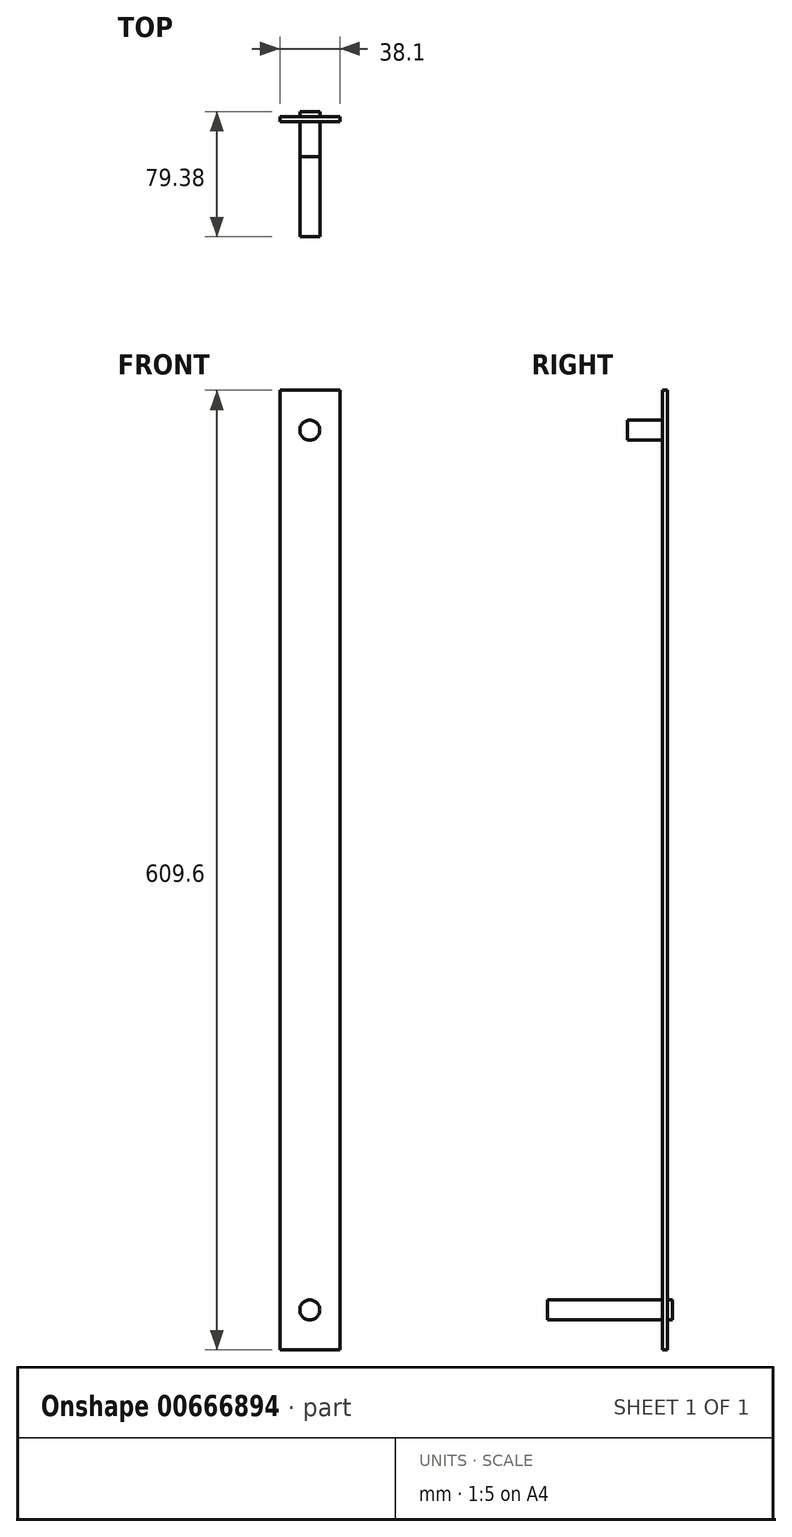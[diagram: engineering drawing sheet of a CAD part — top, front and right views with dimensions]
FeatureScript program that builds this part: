
annotation { "Feature Type Name" : "Feature", "Feature Type Description" : "" }
export const myFeature = defineFeature(function(context is Context, id is Id, definition is map)
    precondition{}
    {
        {
            var Q0;
            Q0=qCreatedBy(makeId("Front.planeOp"),FACE);
            var sketch = newSketch(context, id + "F0", { "sketchPlane" : qUnion([Q0])});
            skLineSegment(sketch, "E0.bottom", {"start": v(0, 0) * mm, "end": v(38.1, 0) * mm});
            skLineSegment(sketch, "E0.top", {"start": v(0, 609.6) * mm, "end": v(38.1, 609.6) * mm});
            skLineSegment(sketch, "E0.left", {"start": v(0, 0) * mm, "end": v(0, 609.6) * mm});
            skLineSegment(sketch, "E0.right", {"start": v(38.1, 0) * mm, "end": v(38.1, 609.6) * mm});
            skLineSegment(sketch, "E1", {"start": v(19.05, 609.6) * mm, "end": v(19.05, 0) * mm, "construction": true});
            skPoint(sketch, "E2", {"position": v(19.05, 25.4) * mm});
            skCircle(sketch, "E3", {"center": v(19.05, 25.4) * mm, "radius": 6.35 * mm});
            skPoint(sketch, "E4", {"position": v(19.05, 584.2) * mm});
            skCircle(sketch, "E5", {"center": v(19.05, 584.2) * mm, "radius": 6.35 * mm});
            skSolve(sketch);
        }
        {
            var Q0;
            Q0=makeQuery(id+"F0.imprint","IMPRINT",FACE,{"disambiguationData":[TD([[makeQuery(id+"F0.imprint","IMPRINT",EDGE,{"derivedFrom":sQuery(id+"F0.wireOp",EDGE,"E0.bottom")}),1.0]])]});
            extrude(context, id + "F1", {"entities" : qUnion([Q0]), "depth" : 3.17 * mm, "offsetDistance" : 25.4 * mm});
        }
        {
            var Q0;
            Q0=makeQuery(id+"F0.imprint","IMPRINT",FACE,{"disambiguationData":[TD([[makeQuery(id+"F0.imprint","IMPRINT",EDGE,{"derivedFrom":sQuery(id+"F0.wireOp",EDGE,"E3")}),1.0]])]});
            extrude(context, id + "F2", {"entities" : qUnion([Q0]), "operationType" : NewBodyOperationType.ADD, "depth" : 76.2 * mm, "offsetDistance" : 25.4 * mm, "hasSecondDirection" : true, "secondDirectionOppositeDirection" : true, "secondDirectionDepth" : 3.17 * mm});
        }
        {
            var Q0;
            Q0=makeQuery(id+"F0.imprint","IMPRINT",FACE,{"disambiguationData":[TD([[makeQuery(id+"F0.imprint","IMPRINT",EDGE,{"derivedFrom":sQuery(id+"F0.wireOp",EDGE,"E5")}),1.0]])]});
            extrude(context, id + "F3", {"entities" : qUnion([Q0]), "operationType" : NewBodyOperationType.ADD, "depth" : 25.4 * mm, "offsetDistance" : 25.4 * mm});
        }
    });
